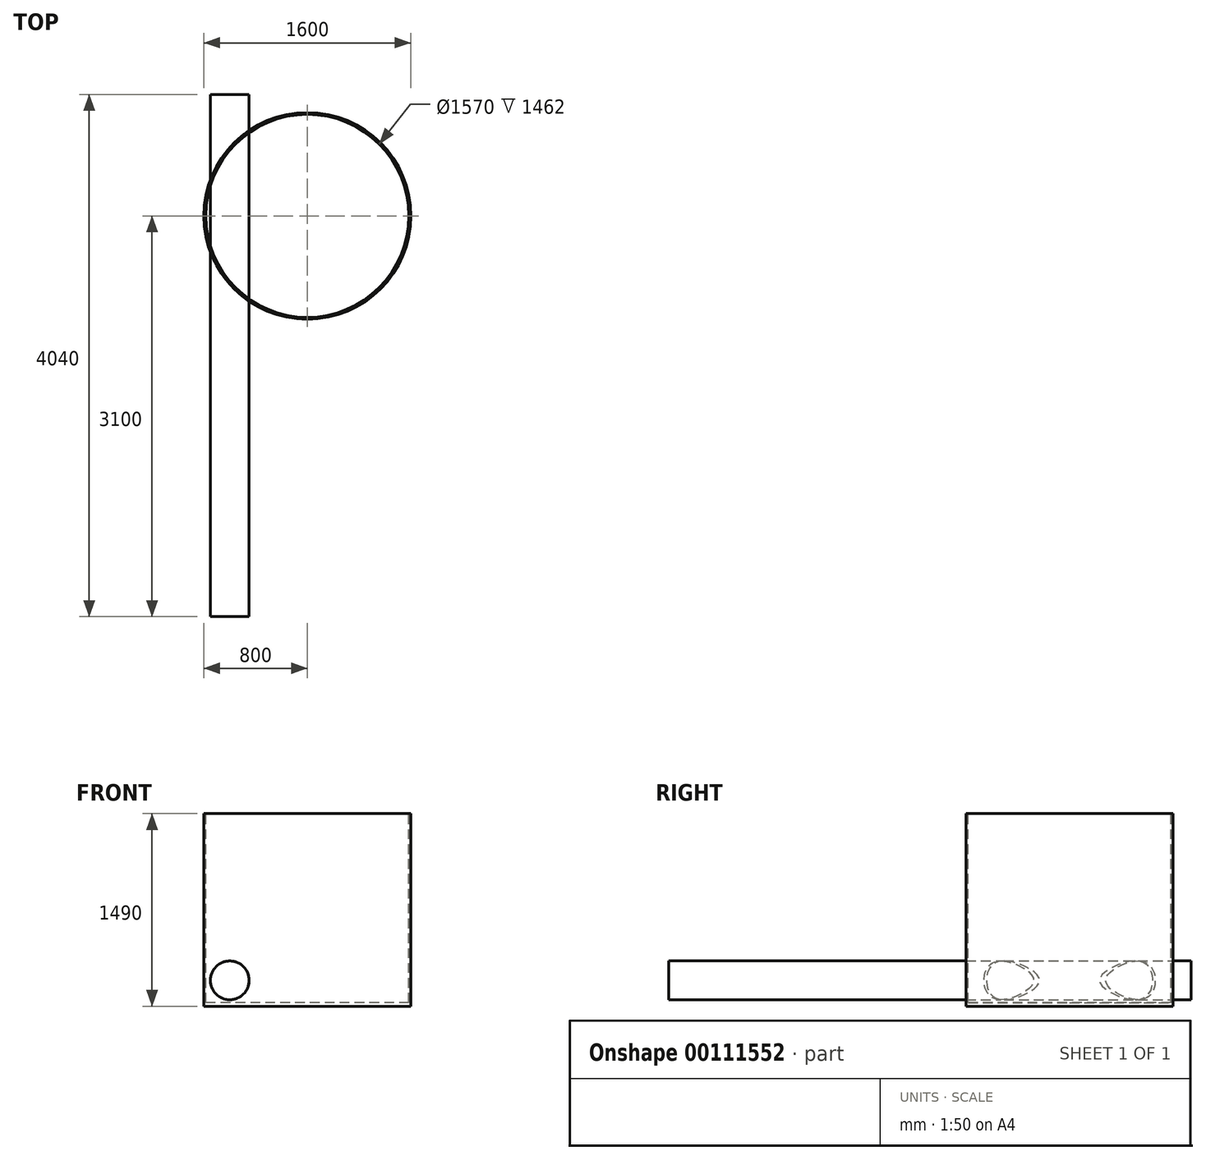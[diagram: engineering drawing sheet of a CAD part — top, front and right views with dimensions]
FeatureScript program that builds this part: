
annotation { "Feature Type Name" : "Feature", "Feature Type Description" : "" }
export const myFeature = defineFeature(function(context is Context, id is Id, definition is map)
    precondition{}
    {
        {
            var Q0;
            Q0=qCreatedBy(makeId("Top.planeOp"),FACE);
            var sketch = newSketch(context, id + "F0", { "sketchPlane" : qUnion([Q0])});
            skCircle(sketch, "E0", {"center": v(0, 0) * mm, "radius": 800 * mm});
            skSolve(sketch);
        }
        {
            var Q0;
            Q0 = qSketchRegion(id + "F0", true);
            extrude(context, id + "F1", {"entities" : qUnion([Q0]), "depth" : (2640 - 1150) * mm});
        }
        {
            var Q0;
            Q0=makeQuery(id+"F1.opExtrude","CAP_FACE",FACE,{"disambiguationData":[OSD([sQuery(id+"F0.wireOp",EDGE,"E0")])],"isStart":false});
            var sketch = newSketch(context, id + "F2", { "sketchPlane" : qUnion([Q0])});
            skCircle(sketch, "E1", {"center": v(0, 0) * mm, "radius": 785 * mm});
            skSolve(sketch);
        }
        {
            var Q0;
            Q0 = qSketchRegion(id + "F2", true);
            extrude(context, id + "F3", {"entities" : qUnion([Q0]), "operationType" : NewBodyOperationType.REMOVE, "oppositeDirection" : true, "depth" : 1462 * mm});
        }
        {
            var Q0;
            Q0=qCreatedBy(makeId("Front.planeOp"),FACE);
            var sketch = newSketch(context, id + "F4", { "sketchPlane" : qUnion([Q0])});
            skCircle(sketch, "E2", {"center": v(-600, 200) * mm, "radius": 150 * mm});
            skLineSegment(sketch, "E3", {"start": v(-800, 0) * mm, "end": v(-800, 627.99) * mm, "construction": true});
            skSolve(sketch);
        }
        {
            var Q0;
            Q0 = qSketchRegion(id + "F4", true);
            extrude(context, id + "F5", {"entities" : qUnion([Q0]), "operationType" : NewBodyOperationType.ADD, "depth" : 3100 * mm, "hasSecondDirection" : true, "secondDirectionOppositeDirection" : true, "secondDirectionDepth" : 940 * mm});
        }
    });
